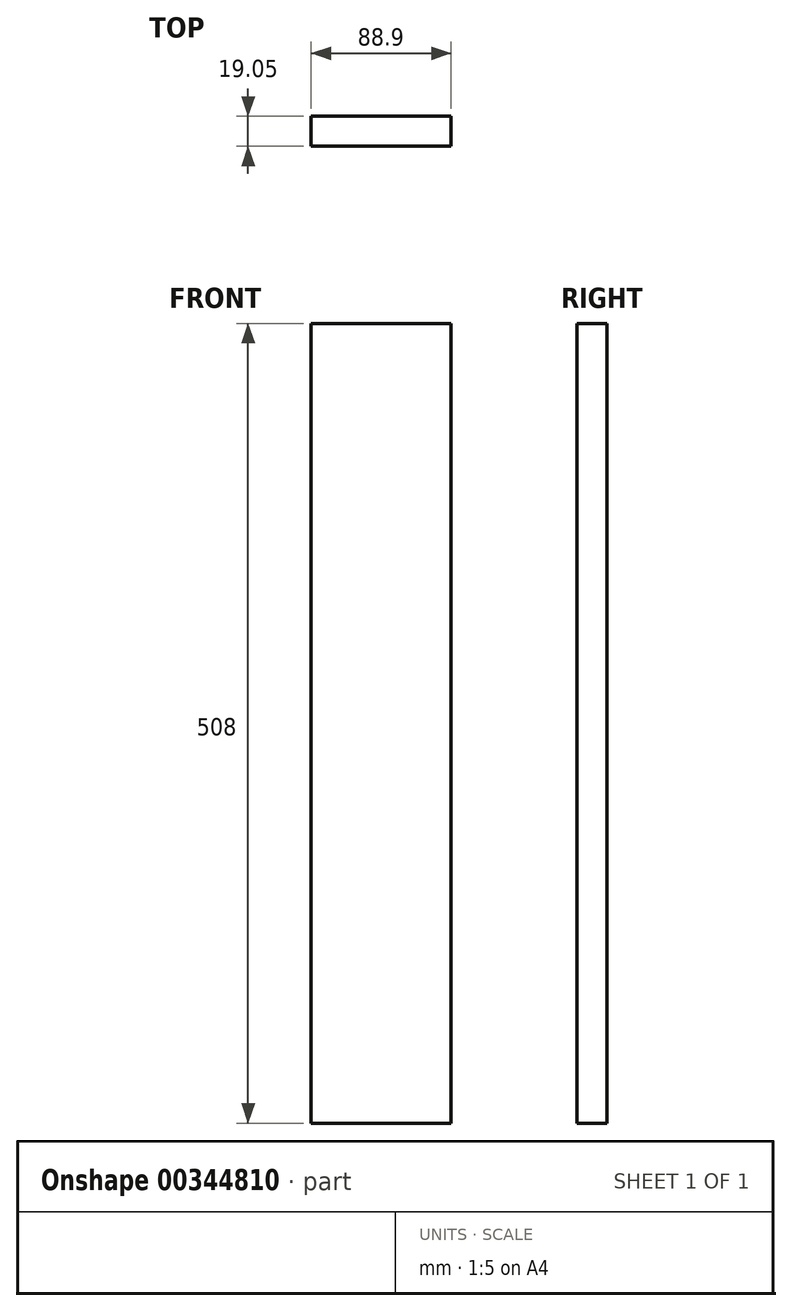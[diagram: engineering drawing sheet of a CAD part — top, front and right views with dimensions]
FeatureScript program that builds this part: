
annotation { "Feature Type Name" : "Feature", "Feature Type Description" : "" }
export const myFeature = defineFeature(function(context is Context, id is Id, definition is map)
    precondition{}
    {
        {
            var Q0;
            Q0=qCreatedBy(makeId("Front.planeOp"),FACE);
            var sketch = newSketch(context, id + "F0", { "sketchPlane" : qUnion([Q0])});
            skLineSegment(sketch, "E0.bottom", {"start": v(0, 0) * mm, "end": v(88.9, 0) * mm});
            skLineSegment(sketch, "E0.top", {"start": v(0, 508) * mm, "end": v(88.9, 508) * mm});
            skLineSegment(sketch, "E0.left", {"start": v(0, 0) * mm, "end": v(0, 508) * mm});
            skLineSegment(sketch, "E0.right", {"start": v(88.9, 0) * mm, "end": v(88.9, 508) * mm});
            skSolve(sketch);
        }
        {
            var Q0;
            Q0=makeQuery(id+"F0.imprint","IMPRINT",FACE,{"disambiguationData":[TD([[makeQuery(id+"F0.imprint","IMPRINT",EDGE,{"derivedFrom":sQuery(id+"F0.wireOp",EDGE,"E0.bottom")}),1.0]])]});
            extrude(context, id + "F1", {"entities" : qUnion([Q0]), "depth" : 19.05 * mm});
        }
    });
